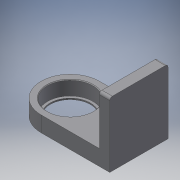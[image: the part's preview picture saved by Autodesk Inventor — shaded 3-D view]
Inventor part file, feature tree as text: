
AUTODESK INVENTOR PART (.ipt)
format: ipt  version: 2018 (Build 220112000, 112)  size: 131,584 bytes
history: native  units: mm
features: extrude x4, sketch x4, chamfer x1, fillet x1
ambient origin geometry x8: Origin, YZ Plane, XZ Plane, XY Plane, X Axis, Y Axis, Z Axis, Center Point
bodies: Solido1 (feature_tree)
feature tree (10):
  extrude  "Estrusione1"  Depth=45.0mm
  extrude  "Estrusione2"  Depth=45.0mm
  extrude  "Estrusione3"  Depth=12.0mm TaperAngle=0.0deg
  chamfer  "Smusso1"  Distance=35.0mm
  extrude  "Estrusione4"  Depth=11.0mm TaperAngle=0.0deg
  fillet  "Raccordo2"  Radius=31.0mm
  sketch  "Schizzo1"
  sketch  "Schizzo2"
  sketch  "Schizzo3"
  sketch  "Schizzo4"
